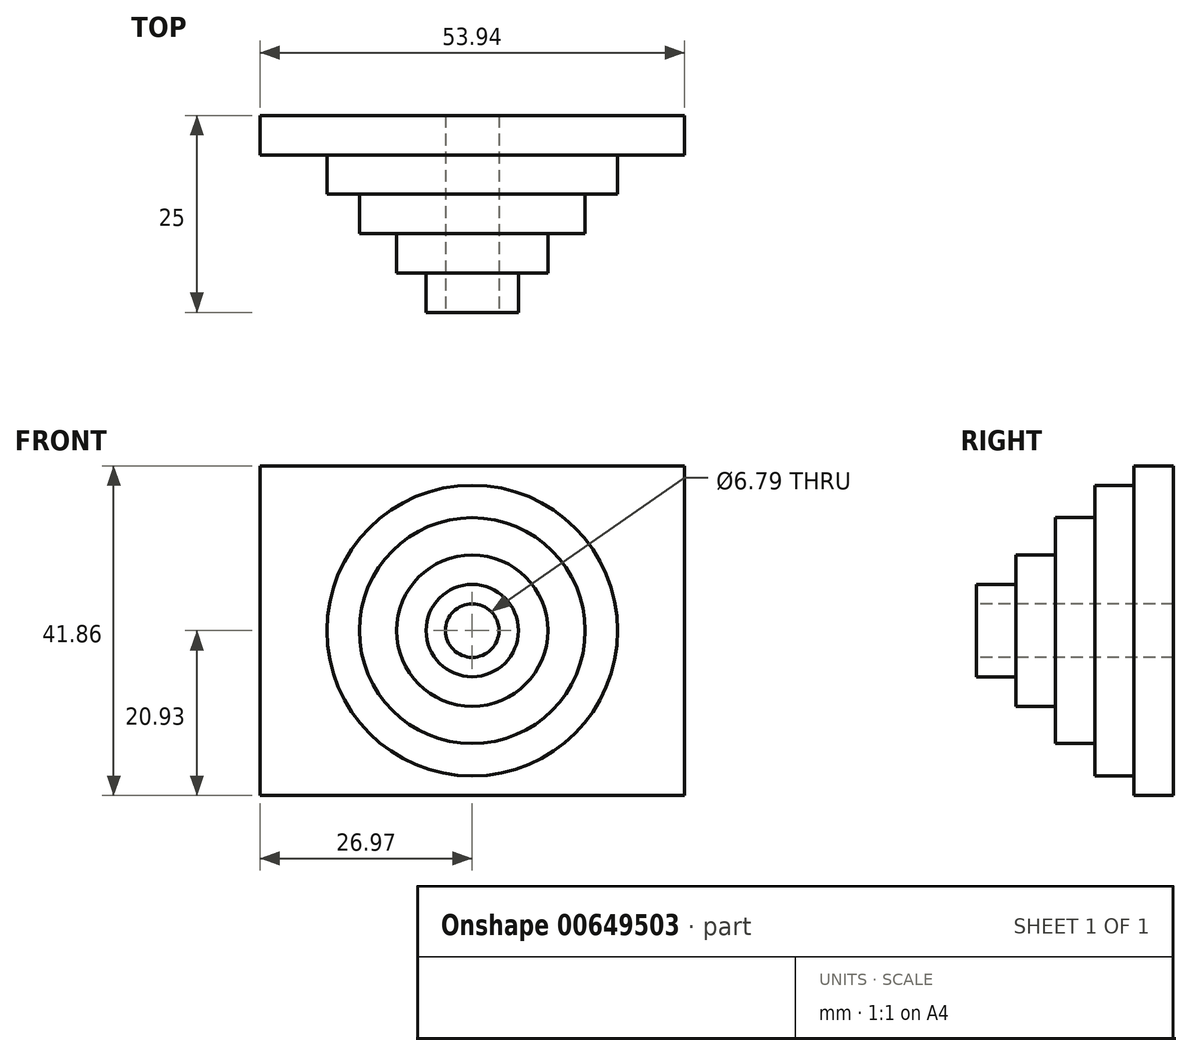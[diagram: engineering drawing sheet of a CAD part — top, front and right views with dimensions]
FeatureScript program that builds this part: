
annotation { "Feature Type Name" : "Feature", "Feature Type Description" : "" }
export const myFeature = defineFeature(function(context is Context, id is Id, definition is map)
    precondition{}
    {
        {
            var Q0;
            Q0=qCreatedBy(makeId("Front.planeOp"),FACE);
            var sketch = newSketch(context, id + "F0", { "sketchPlane" : qUnion([Q0])});
            skLineSegment(sketch, "E0.bottom", {"start": v(26.97, -20.93) * mm, "end": v(-26.97, -20.93) * mm});
            skLineSegment(sketch, "E0.top", {"start": v(26.97, 20.93) * mm, "end": v(-26.97, 20.93) * mm});
            skLineSegment(sketch, "E0.left", {"start": v(26.97, -20.93) * mm, "end": v(26.97, 20.93) * mm});
            skLineSegment(sketch, "E0.right", {"start": v(-26.97, -20.93) * mm, "end": v(-26.97, 20.93) * mm});
            skPoint(sketch, "E0.middle", {"position": v(0, 0) * mm});
            skSolve(sketch);
        }
        {
            var Q0;
            Q0=makeQuery(id+"F0.imprint","IMPRINT",FACE,{"disambiguationData":[TD([[makeQuery(id+"F0.imprint","IMPRINT",EDGE,{"derivedFrom":sQuery(id+"F0.wireOp",EDGE,"E0.bottom")}),-1.0]])]});
            extrude(context, id + "F1", {"entities" : qUnion([Q0]), "depth" : 5 * mm, "offsetDistance" : 25 * mm});
        }
        {
            var Q0;
            Q0=makeQuery(id+"F1.opExtrude","CAP_FACE",FACE,{"disambiguationData":[OSD([sQuery(id+"F0.wireOp",EDGE,"E0.bottom"),sQuery(id+"F0.wireOp",EDGE,"E0.top"),sQuery(id+"F0.wireOp",EDGE,"E0.left"),sQuery(id+"F0.wireOp",EDGE,"E0.right")])],"isStart":false});
            var sketch = newSketch(context, id + "F2", { "sketchPlane" : qUnion([Q0])});
            skCircle(sketch, "E1", {"center": v(0, 0) * mm, "radius": 18.47 * mm});
            skSolve(sketch);
        }
        {
            var Q0;
            Q0=makeQuery(id+"F2.imprint","IMPRINT",FACE,{"disambiguationData":[TD([[makeQuery(id+"F2.imprint","IMPRINT",EDGE,{"derivedFrom":sQuery(id+"F2.wireOp",EDGE,"E1")}),1.0]])]});
            extrude(context, id + "F3", {"entities" : qUnion([Q0]), "operationType" : NewBodyOperationType.ADD, "depth" : 5 * mm, "offsetDistance" : 25 * mm});
        }
        {
            var Q0;
            Q0=makeQuery(id+"F3.opExtrude","CAP_FACE",FACE,{"disambiguationData":[OSD([sQuery(id+"F2.wireOp",EDGE,"E1")])],"isStart":false});
            var sketch = newSketch(context, id + "F4", { "sketchPlane" : qUnion([Q0])});
            skCircle(sketch, "E2", {"center": v(0, 0) * mm, "radius": 14.34 * mm});
            skSolve(sketch);
        }
        {
            var Q0;
            Q0=makeQuery(id+"F4.imprint","IMPRINT",FACE,{"disambiguationData":[TD([[makeQuery(id+"F4.imprint","IMPRINT",EDGE,{"derivedFrom":sQuery(id+"F4.wireOp",EDGE,"E2")}),1.0]])]});
            extrude(context, id + "F5", {"entities" : qUnion([Q0]), "operationType" : NewBodyOperationType.ADD, "depth" : 5 * mm, "offsetDistance" : 25 * mm});
        }
        {
            var Q0;
            Q0=makeQuery(id+"F5.opExtrude","CAP_FACE",FACE,{"disambiguationData":[OSD([sQuery(id+"F4.wireOp",EDGE,"E2")])],"isStart":false});
            var sketch = newSketch(context, id + "F6", { "sketchPlane" : qUnion([Q0])});
            skCircle(sketch, "E3", {"center": v(0, 0) * mm, "radius": 9.61 * mm});
            skSolve(sketch);
        }
        {
            var Q0;
            Q0=makeQuery(id+"F6.imprint","IMPRINT",FACE,{"disambiguationData":[TD([[makeQuery(id+"F6.imprint","IMPRINT",EDGE,{"derivedFrom":sQuery(id+"F6.wireOp",EDGE,"E3")}),1.0]])]});
            extrude(context, id + "F7", {"entities" : qUnion([Q0]), "operationType" : NewBodyOperationType.ADD, "depth" : 5 * mm, "offsetDistance" : 25 * mm});
        }
        {
            var Q0;
            Q0=makeQuery(id+"F7.opExtrude","CAP_FACE",FACE,{"disambiguationData":[OSD([sQuery(id+"F6.wireOp",EDGE,"E3")])],"isStart":false});
            var sketch = newSketch(context, id + "F8", { "sketchPlane" : qUnion([Q0])});
            skCircle(sketch, "E4", {"center": v(0, 0) * mm, "radius": 5.86 * mm});
            skSolve(sketch);
        }
        {
            var Q0;
            Q0=makeQuery(id+"F8.imprint","IMPRINT",FACE,{"disambiguationData":[TD([[makeQuery(id+"F8.imprint","IMPRINT",EDGE,{"derivedFrom":sQuery(id+"F8.wireOp",EDGE,"E4")}),1.0]])]});
            extrude(context, id + "F9", {"entities" : qUnion([Q0]), "operationType" : NewBodyOperationType.ADD, "depth" : 5 * mm, "offsetDistance" : 25 * mm});
        }
        {
            var Q0;
            Q0=makeQuery(id+"F9.opExtrude","CAP_FACE",FACE,{"disambiguationData":[OSD([sQuery(id+"F8.wireOp",EDGE,"E4")])],"isStart":false});
            var sketch = newSketch(context, id + "F10", { "sketchPlane" : qUnion([Q0])});
            skCircle(sketch, "E5", {"center": v(0, 0) * mm, "radius": 3.4 * mm});
            skSolve(sketch);
        }
        {
            var Q0;
            Q0=makeQuery(id+"F10.imprint","IMPRINT",FACE,{"disambiguationData":[TD([[makeQuery(id+"F10.imprint","IMPRINT",EDGE,{"derivedFrom":sQuery(id+"F10.wireOp",EDGE,"E5")}),1.0]])]});
            extrude(context, id + "F11", {"entities" : qUnion([Q0]), "operationType" : NewBodyOperationType.REMOVE, "endBound" : BoundingType.THROUGH_ALL, "oppositeDirection" : true, "depth" : 25 * mm, "offsetDistance" : 25 * mm});
        }
    });
